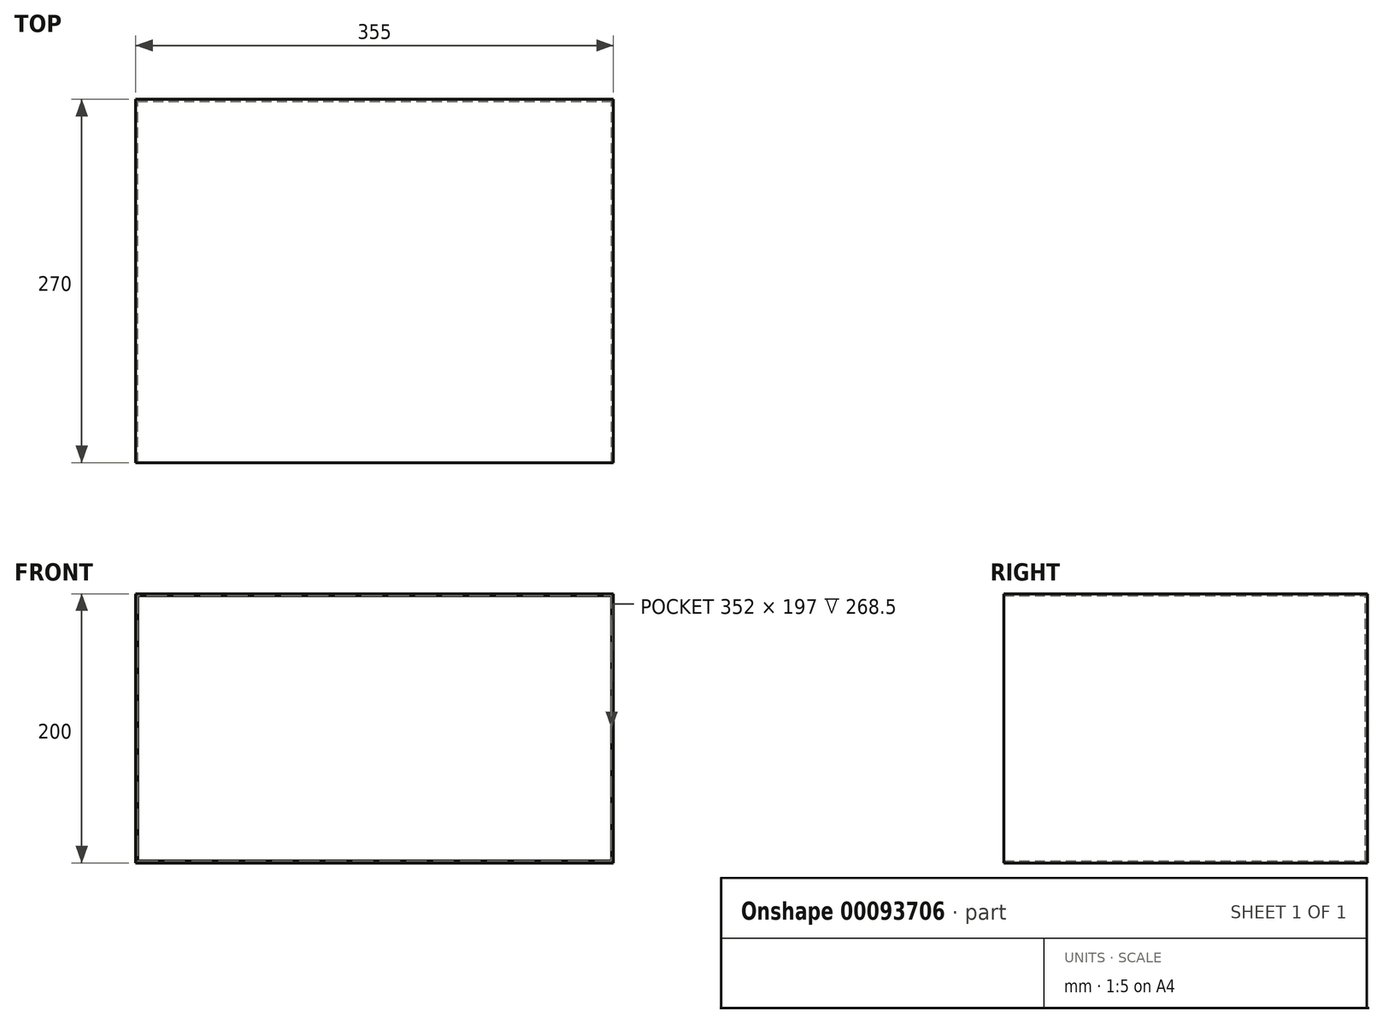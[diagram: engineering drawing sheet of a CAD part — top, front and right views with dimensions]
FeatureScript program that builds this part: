
annotation { "Feature Type Name" : "Feature", "Feature Type Description" : "" }
export const myFeature = defineFeature(function(context is Context, id is Id, definition is map)
    precondition{}
    {
        {
            var Q0;
            Q0=qCreatedBy(makeId("Right.planeOp"),FACE);
            var sketch = newSketch(context, id + "F0", { "sketchPlane" : qUnion([Q0])});
            skLineSegment(sketch, "E0.bottom", {"start": v(0, 0) * mm, "end": v(270, 0) * mm});
            skLineSegment(sketch, "E0.top", {"start": v(0, 200) * mm, "end": v(270, 200) * mm});
            skLineSegment(sketch, "E0.left", {"start": v(0, 0) * mm, "end": v(0, 200) * mm});
            skLineSegment(sketch, "E0.right", {"start": v(270, 0) * mm, "end": v(270, 200) * mm});
            skSolve(sketch);
        }
        {
            var Q0;
            Q0=makeQuery(id+"F0.imprint","IMPRINT",FACE,{"disambiguationData":[TD([[makeQuery(id+"F0.imprint","IMPRINT",EDGE,{"derivedFrom":sQuery(id+"F0.wireOp",EDGE,"E0.bottom")}),1.0]])]});
            extrude(context, id + "F1", {"entities" : qUnion([Q0]), "oppositeDirection" : true, "depth" : 355 * mm, "offsetDistance" : 25 * mm});
        }
        {
            var Q0;
            Q0=makeQuery(id+"F1.opExtrude","SWEPT_FACE",FACE,{"disambiguationData":[OSD([sQuery(id+"F0.wireOp",EDGE,"E0.left")])]});
            shell(context, id + "F2", {"entities" : qUnion([Q0]), "thickness" : 1.5 * mm});
        }
    });
